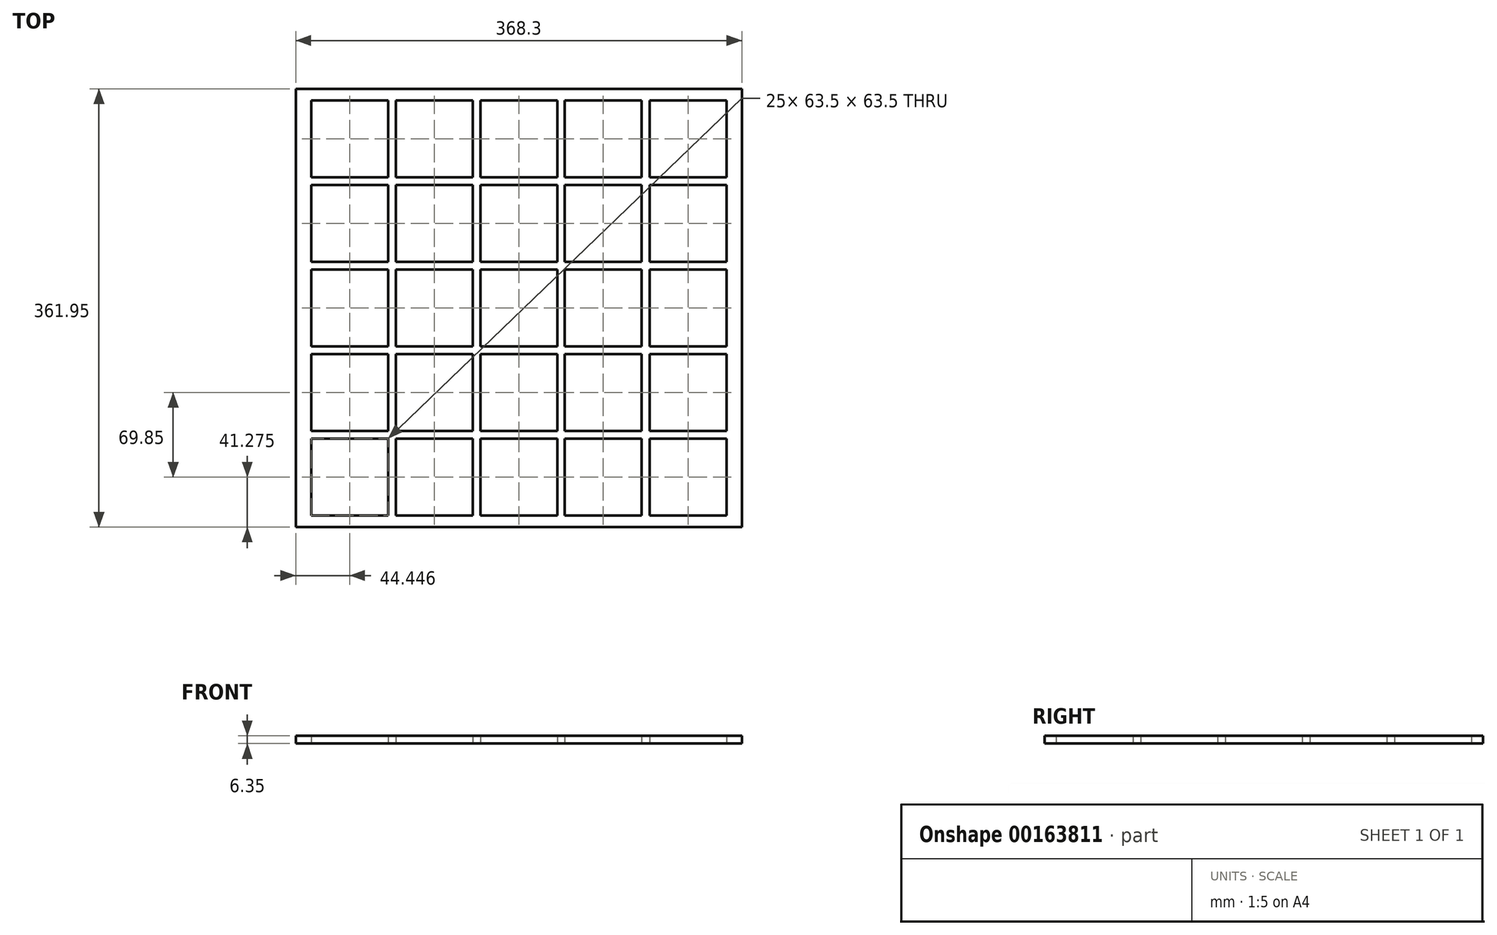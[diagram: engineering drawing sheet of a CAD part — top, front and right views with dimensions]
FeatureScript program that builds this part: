
annotation { "Feature Type Name" : "Feature", "Feature Type Description" : "" }
export const myFeature = defineFeature(function(context is Context, id is Id, definition is map)
    precondition{}
    {
        {
            var Q0;
            Q0=qCreatedBy(makeId("Top.planeOp"),FACE);
            var sketch = newSketch(context, id + "F0", { "sketchPlane" : qUnion([Q0])});
            skLineSegment(sketch, "E0.top", {"start": v(193.75, -175.68) * mm, "end": v(-174.55, -175.68) * mm});
            skLineSegment(sketch, "E0.left", {"start": v(193.75, 186.27) * mm, "end": v(193.75, -175.68) * mm});
            skLineSegment(sketch, "E0.right", {"start": v(-174.55, 186.27) * mm, "end": v(-174.55, -175.68) * mm});
            skLineSegment(sketch, "E1", {"start": v(-174.55, 186.27) * mm, "end": v(193.75, 186.27) * mm});
            skLineSegment(sketch, "E2.bottom", {"start": v(-98.35, -166.16) * mm, "end": v(-161.85, -166.16) * mm});
            skLineSegment(sketch, "E2.top", {"start": v(-98.35, -102.66) * mm, "end": v(-161.85, -102.66) * mm});
            skLineSegment(sketch, "E2.left", {"start": v(-98.35, -166.16) * mm, "end": v(-98.35, -102.66) * mm});
            skLineSegment(sketch, "E2.right", {"start": v(-161.85, -166.16) * mm, "end": v(-161.85, -102.66) * mm});
            skPoint(sketch, "E2.middle", {"position": v(-130.1, -134.4) * mm});
            skLineSegment(sketch, "E3.0.1.0", {"start": v(-98.35, -32.8) * mm, "end": v(-161.85, -32.8) * mm});
            skLineSegment(sketch, "E3.0.1.1", {"start": v(-98.35, -96.3) * mm, "end": v(-98.35, -32.8) * mm});
            skLineSegment(sketch, "E3.0.1.2", {"start": v(-98.35, -96.3) * mm, "end": v(-161.85, -96.3) * mm});
            skLineSegment(sketch, "E3.0.1.3", {"start": v(-161.85, -96.3) * mm, "end": v(-161.85, -32.8) * mm});
            skLineSegment(sketch, "E3.0.2.0", {"start": v(-98.35, 37.04) * mm, "end": v(-161.85, 37.04) * mm});
            skLineSegment(sketch, "E3.0.2.1", {"start": v(-98.35, -26.46) * mm, "end": v(-98.35, 37.04) * mm});
            skLineSegment(sketch, "E3.0.2.2", {"start": v(-98.35, -26.46) * mm, "end": v(-161.85, -26.46) * mm});
            skLineSegment(sketch, "E3.0.2.3", {"start": v(-161.85, -26.46) * mm, "end": v(-161.85, 37.04) * mm});
            skLineSegment(sketch, "E3.0.3.0", {"start": v(-98.35, 106.9) * mm, "end": v(-161.85, 106.9) * mm});
            skLineSegment(sketch, "E3.0.3.1", {"start": v(-98.35, 43.4) * mm, "end": v(-98.35, 106.9) * mm});
            skLineSegment(sketch, "E3.0.3.2", {"start": v(-98.35, 43.4) * mm, "end": v(-161.85, 43.4) * mm});
            skLineSegment(sketch, "E3.0.3.3", {"start": v(-161.85, 43.4) * mm, "end": v(-161.85, 106.9) * mm});
            skLineSegment(sketch, "E3.0.4.0", {"start": v(-98.35, 176.74) * mm, "end": v(-161.85, 176.74) * mm});
            skLineSegment(sketch, "E3.0.4.1", {"start": v(-98.35, 113.24) * mm, "end": v(-98.35, 176.74) * mm});
            skLineSegment(sketch, "E3.0.4.2", {"start": v(-98.35, 113.24) * mm, "end": v(-161.85, 113.24) * mm});
            skLineSegment(sketch, "E3.0.4.3", {"start": v(-161.85, 113.24) * mm, "end": v(-161.85, 176.74) * mm});
            skLineSegment(sketch, "E3.1.0.0", {"start": v(-28.5, -102.66) * mm, "end": v(-92, -102.66) * mm});
            skLineSegment(sketch, "E3.1.0.1", {"start": v(-28.5, -166.16) * mm, "end": v(-28.5, -102.66) * mm});
            skLineSegment(sketch, "E3.1.0.2", {"start": v(-28.5, -166.16) * mm, "end": v(-92, -166.16) * mm});
            skLineSegment(sketch, "E3.1.0.3", {"start": v(-92, -166.16) * mm, "end": v(-92, -102.66) * mm});
            skLineSegment(sketch, "E3.1.1.0", {"start": v(-28.5, -32.8) * mm, "end": v(-92, -32.8) * mm});
            skLineSegment(sketch, "E3.1.1.1", {"start": v(-28.5, -96.3) * mm, "end": v(-28.5, -32.8) * mm});
            skLineSegment(sketch, "E3.1.1.2", {"start": v(-28.5, -96.3) * mm, "end": v(-92, -96.3) * mm});
            skLineSegment(sketch, "E3.1.1.3", {"start": v(-92, -96.3) * mm, "end": v(-92, -32.8) * mm});
            skLineSegment(sketch, "E3.1.2.0", {"start": v(-28.5, 37.04) * mm, "end": v(-92, 37.04) * mm});
            skLineSegment(sketch, "E3.1.2.1", {"start": v(-28.5, -26.46) * mm, "end": v(-28.5, 37.04) * mm});
            skLineSegment(sketch, "E3.1.2.2", {"start": v(-28.5, -26.46) * mm, "end": v(-92, -26.46) * mm});
            skLineSegment(sketch, "E3.1.2.3", {"start": v(-92, -26.46) * mm, "end": v(-92, 37.04) * mm});
            skLineSegment(sketch, "E3.1.3.0", {"start": v(-28.5, 106.9) * mm, "end": v(-92, 106.9) * mm});
            skLineSegment(sketch, "E3.1.3.1", {"start": v(-28.5, 43.4) * mm, "end": v(-28.5, 106.9) * mm});
            skLineSegment(sketch, "E3.1.3.2", {"start": v(-28.5, 43.4) * mm, "end": v(-92, 43.4) * mm});
            skLineSegment(sketch, "E3.1.3.3", {"start": v(-92, 43.4) * mm, "end": v(-92, 106.9) * mm});
            skLineSegment(sketch, "E3.1.4.0", {"start": v(-28.5, 176.74) * mm, "end": v(-92, 176.74) * mm});
            skLineSegment(sketch, "E3.1.4.1", {"start": v(-28.5, 113.24) * mm, "end": v(-28.5, 176.74) * mm});
            skLineSegment(sketch, "E3.1.4.2", {"start": v(-28.5, 113.24) * mm, "end": v(-92, 113.24) * mm});
            skLineSegment(sketch, "E3.1.4.3", {"start": v(-92, 113.24) * mm, "end": v(-92, 176.74) * mm});
            skLineSegment(sketch, "E3.2.0.0", {"start": v(41.35, -102.66) * mm, "end": v(-22.15, -102.66) * mm});
            skLineSegment(sketch, "E3.2.0.1", {"start": v(41.35, -166.16) * mm, "end": v(41.35, -102.66) * mm});
            skLineSegment(sketch, "E3.2.0.2", {"start": v(41.35, -166.16) * mm, "end": v(-22.15, -166.16) * mm});
            skLineSegment(sketch, "E3.2.0.3", {"start": v(-22.15, -166.16) * mm, "end": v(-22.15, -102.66) * mm});
            skLineSegment(sketch, "E3.2.1.0", {"start": v(41.35, -32.8) * mm, "end": v(-22.15, -32.8) * mm});
            skLineSegment(sketch, "E3.2.1.1", {"start": v(41.35, -96.3) * mm, "end": v(41.35, -32.8) * mm});
            skLineSegment(sketch, "E3.2.1.2", {"start": v(41.35, -96.3) * mm, "end": v(-22.15, -96.3) * mm});
            skLineSegment(sketch, "E3.2.1.3", {"start": v(-22.15, -96.3) * mm, "end": v(-22.15, -32.8) * mm});
            skLineSegment(sketch, "E3.2.2.0", {"start": v(41.35, 37.04) * mm, "end": v(-22.15, 37.04) * mm});
            skLineSegment(sketch, "E3.2.2.1", {"start": v(41.35, -26.46) * mm, "end": v(41.35, 37.04) * mm});
            skLineSegment(sketch, "E3.2.2.2", {"start": v(41.35, -26.46) * mm, "end": v(-22.15, -26.46) * mm});
            skLineSegment(sketch, "E3.2.2.3", {"start": v(-22.15, -26.46) * mm, "end": v(-22.15, 37.04) * mm});
            skLineSegment(sketch, "E3.2.3.0", {"start": v(41.35, 106.9) * mm, "end": v(-22.15, 106.9) * mm});
            skLineSegment(sketch, "E3.2.3.1", {"start": v(41.35, 43.4) * mm, "end": v(41.35, 106.9) * mm});
            skLineSegment(sketch, "E3.2.3.2", {"start": v(41.35, 43.4) * mm, "end": v(-22.15, 43.4) * mm});
            skLineSegment(sketch, "E3.2.3.3", {"start": v(-22.15, 43.4) * mm, "end": v(-22.15, 106.9) * mm});
            skLineSegment(sketch, "E3.2.4.0", {"start": v(41.35, 176.74) * mm, "end": v(-22.15, 176.74) * mm});
            skLineSegment(sketch, "E3.2.4.1", {"start": v(41.35, 113.24) * mm, "end": v(41.35, 176.74) * mm});
            skLineSegment(sketch, "E3.2.4.2", {"start": v(41.35, 113.24) * mm, "end": v(-22.15, 113.24) * mm});
            skLineSegment(sketch, "E3.2.4.3", {"start": v(-22.15, 113.24) * mm, "end": v(-22.15, 176.74) * mm});
            skLineSegment(sketch, "E3.3.0.0", {"start": v(111.2, -102.66) * mm, "end": v(47.7, -102.66) * mm});
            skLineSegment(sketch, "E3.3.0.1", {"start": v(111.2, -166.16) * mm, "end": v(111.2, -102.66) * mm});
            skLineSegment(sketch, "E3.3.0.2", {"start": v(111.2, -166.16) * mm, "end": v(47.7, -166.16) * mm});
            skLineSegment(sketch, "E3.3.0.3", {"start": v(47.7, -166.16) * mm, "end": v(47.7, -102.66) * mm});
            skLineSegment(sketch, "E3.3.1.0", {"start": v(111.2, -32.8) * mm, "end": v(47.7, -32.8) * mm});
            skLineSegment(sketch, "E3.3.1.1", {"start": v(111.2, -96.3) * mm, "end": v(111.2, -32.8) * mm});
            skLineSegment(sketch, "E3.3.1.2", {"start": v(111.2, -96.3) * mm, "end": v(47.7, -96.3) * mm});
            skLineSegment(sketch, "E3.3.1.3", {"start": v(47.7, -96.3) * mm, "end": v(47.7, -32.8) * mm});
            skLineSegment(sketch, "E3.3.2.0", {"start": v(111.2, 37.04) * mm, "end": v(47.7, 37.04) * mm});
            skLineSegment(sketch, "E3.3.2.1", {"start": v(111.2, -26.46) * mm, "end": v(111.2, 37.04) * mm});
            skLineSegment(sketch, "E3.3.2.2", {"start": v(111.2, -26.46) * mm, "end": v(47.7, -26.46) * mm});
            skLineSegment(sketch, "E3.3.2.3", {"start": v(47.7, -26.46) * mm, "end": v(47.7, 37.04) * mm});
            skLineSegment(sketch, "E3.3.3.0", {"start": v(111.2, 106.9) * mm, "end": v(47.7, 106.9) * mm});
            skLineSegment(sketch, "E3.3.3.1", {"start": v(111.2, 43.4) * mm, "end": v(111.2, 106.9) * mm});
            skLineSegment(sketch, "E3.3.3.2", {"start": v(111.2, 43.4) * mm, "end": v(47.7, 43.4) * mm});
            skLineSegment(sketch, "E3.3.3.3", {"start": v(47.7, 43.4) * mm, "end": v(47.7, 106.9) * mm});
            skLineSegment(sketch, "E3.3.4.0", {"start": v(111.2, 176.74) * mm, "end": v(47.7, 176.74) * mm});
            skLineSegment(sketch, "E3.3.4.1", {"start": v(111.2, 113.24) * mm, "end": v(111.2, 176.74) * mm});
            skLineSegment(sketch, "E3.3.4.2", {"start": v(111.2, 113.24) * mm, "end": v(47.7, 113.24) * mm});
            skLineSegment(sketch, "E3.3.4.3", {"start": v(47.7, 113.24) * mm, "end": v(47.7, 176.74) * mm});
            skLineSegment(sketch, "E3.4.0.0", {"start": v(181.05, -102.66) * mm, "end": v(117.55, -102.66) * mm});
            skLineSegment(sketch, "E3.4.0.1", {"start": v(181.05, -166.16) * mm, "end": v(181.05, -102.66) * mm});
            skLineSegment(sketch, "E3.4.0.2", {"start": v(181.05, -166.16) * mm, "end": v(117.55, -166.16) * mm});
            skLineSegment(sketch, "E3.4.0.3", {"start": v(117.55, -166.16) * mm, "end": v(117.55, -102.66) * mm});
            skLineSegment(sketch, "E3.4.1.0", {"start": v(181.05, -32.8) * mm, "end": v(117.55, -32.8) * mm});
            skLineSegment(sketch, "E3.4.1.1", {"start": v(181.05, -96.3) * mm, "end": v(181.05, -32.8) * mm});
            skLineSegment(sketch, "E3.4.1.2", {"start": v(181.05, -96.3) * mm, "end": v(117.55, -96.3) * mm});
            skLineSegment(sketch, "E3.4.1.3", {"start": v(117.55, -96.3) * mm, "end": v(117.55, -32.8) * mm});
            skLineSegment(sketch, "E3.4.2.0", {"start": v(181.05, 37.04) * mm, "end": v(117.55, 37.04) * mm});
            skLineSegment(sketch, "E3.4.2.1", {"start": v(181.05, -26.46) * mm, "end": v(181.05, 37.04) * mm});
            skLineSegment(sketch, "E3.4.2.2", {"start": v(181.05, -26.46) * mm, "end": v(117.55, -26.46) * mm});
            skLineSegment(sketch, "E3.4.2.3", {"start": v(117.55, -26.46) * mm, "end": v(117.55, 37.04) * mm});
            skLineSegment(sketch, "E3.4.3.0", {"start": v(181.05, 106.9) * mm, "end": v(117.55, 106.9) * mm});
            skLineSegment(sketch, "E3.4.3.1", {"start": v(181.05, 43.4) * mm, "end": v(181.05, 106.9) * mm});
            skLineSegment(sketch, "E3.4.3.2", {"start": v(181.05, 43.4) * mm, "end": v(117.55, 43.4) * mm});
            skLineSegment(sketch, "E3.4.3.3", {"start": v(117.55, 43.4) * mm, "end": v(117.55, 106.9) * mm});
            skLineSegment(sketch, "E3.4.4.0", {"start": v(181.05, 176.74) * mm, "end": v(117.55, 176.74) * mm});
            skLineSegment(sketch, "E3.4.4.1", {"start": v(181.05, 113.24) * mm, "end": v(181.05, 176.74) * mm});
            skLineSegment(sketch, "E3.4.4.2", {"start": v(181.05, 113.24) * mm, "end": v(117.55, 113.24) * mm});
            skLineSegment(sketch, "E3.4.4.3", {"start": v(117.55, 113.24) * mm, "end": v(117.55, 176.74) * mm});
            skLineSegment(sketch, "E3.direction1", {"start": v(-161.85, -102.66) * mm, "end": v(-92, -102.66) * mm, "construction": true});
            skLineSegment(sketch, "E3.direction2", {"start": v(-161.85, -102.66) * mm, "end": v(-161.85, -32.8) * mm, "construction": true});
            skSolve(sketch);
        }
        {
            var Q0;
            Q0 = qSketchRegion(id + "F0", true);
            extrude(context, id + "F1", {"entities" : qUnion([Q0]), "depth" : 6.35 * mm});
        }
    });
